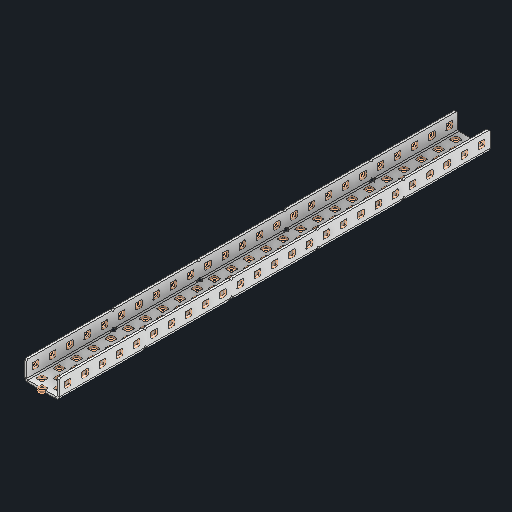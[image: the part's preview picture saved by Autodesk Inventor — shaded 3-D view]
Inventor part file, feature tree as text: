
AUTODESK INVENTOR PART (.ipt)
format: ipt  version: 2024 (Build 280153000, 153)  size: 2,048,000 bytes
history: native  units: in
note: dims shown in document units (in); Inventor stores cm internally (conversion verified against a paired STEP export)
features: other x256, sketch x5, sheet_metal_op x1
ambient origin geometry x8: Origin, YZ Plane, XZ Plane, XY Plane, X Axis, Y Axis, Z Axis, Center Point
bodies: Solid1 (feature_tree)
feature tree (262):
  other  "Alu C 1x2x1x25.ipt"
  other  "Solid1::Alu C 1x2x1x25.ipt"
  other  "TaggingFeature1"
  sketch  "Sketch1"  dims[d0=0.3937in]
  sketch  "Sketch2"  dims[d1=0.0625in]
  sketch  "Sketch3"
  other  "Flange Pattern Sketch"
  sketch  "Sketch9"
  sheet_metal_op  "Body Pattern Sketch"
  other  "Arc Length"
  sketch  "Sketch14"
  other  "Flange Pattern Plane"
  other  "Srf1"
  other  "Srf2"
  other  "Srf3"
  other  "Srf4"
  other  "Srf5"
  other  "Srf6"
  other  "Srf7"
  other  "Srf8"
  other  "Srf9"
  other  "Srf10"
  other  "Srf11"
  other  "Srf12"
  other  "Srf13"
  other  "Srf14"
  other  "Srf15"
  other  "Srf16"
  other  "Srf17"
  other  "Srf18"
  other  "Srf19"
  other  "Srf20"
  other  "Srf21"
  other  "Srf22"
  other  "Srf23"
  other  "Srf24"
  other  "Srf25"
  other  "Srf26"
  other  "Srf27"
  other  "Srf28"
  other  "Srf29"
  other  "Srf30"
  other  "Srf31"
  other  "Srf32"
  other  "Srf33"
  other  "Srf34"
  other  "Srf35"
  other  "Srf36"
  other  "Srf37"
  other  "Srf38"
  other  "Srf39"
  other  "Srf40"
  other  "Srf41"
  other  "Srf42"
  other  "Srf43"
  other  "Srf44"
  other  "Srf45"
  other  "Srf46"
  other  "Srf47"
  other  "Srf48"
  other  "Srf49"
  other  "Srf50"
  other  "Srf51"
  other  "Srf52"
  other  "Srf53"
  other  "Srf54"
  other  "Srf55"
  other  "Srf56"
  other  "Srf57"
  other  "Srf58"
  other  "Srf59"
  other  "Srf60"
  other  "Srf61"
  other  "Srf62"
  other  "Srf63"
  other  "Srf64"
  other  "Srf65"
  other  "Srf66"
  other  "Srf67"
  other  "Srf68"
  other  "Srf69"
  other  "Srf70"
  other  "Srf71"
  other  "Srf72"
  other  "Srf73"
  other  "Srf74"
  other  "Srf75"
  other  "Srf76"
  other  "Srf77"
  other  "Srf78"
  other  "Srf79"
  other  "Srf80"
  other  "Srf81"
  other  "Srf82"
  other  "Srf83"
  other  "Srf84"
  other  "Srf85"
  other  "Srf86"
  other  "Srf87"
  other  "Srf88"
  other  "Srf89"
  other  "Srf90"
  other  "Srf91"
  other  "Srf92"
  other  "Srf93"
  other  "Srf94"
  other  "Srf95"
  other  "Srf96"
  other  "Srf97"
  other  "Srf98"
  other  "Srf99"
  other  "Srf100"
  other  "Srf101"
  other  "Srf102"
  other  "Srf103"
  other  "Srf104"
  other  "Srf105"
  other  "Srf106"
  other  "Srf107"
  other  "Srf108"
  other  "Srf109"
  other  "Srf110"
  other  "Srf111"
  other  "Srf112"
  other  "Srf113"
  other  "Srf114"
  other  "Srf115"
  other  "Srf116"
  other  "Srf117"
  other  "Srf118"
  other  "Srf119"
  other  "Srf120"
  other  "Srf121"
  other  "Srf122"
  other  "Srf123"
  other  "Srf124"
  other  "Srf125"
  other  "Srf1::Derived"
  other  "Srf2::Derived"
  other  "Srf823::Derived"
  other  "Srf824::Derived"
  other  "Srf825::Derived"
  other  "Srf826::Derived"
  other  "Srf827::Derived"
  other  "Srf828::Derived"
  other  "Srf829::Derived"
  other  "Srf922::Derived"
  other  "Srf923::Derived"
  other  "Srf924::Derived"
  other  "Srf925::Derived"
  other  "Srf926::Derived"
  other  "Srf1143::Derived"
  other  "Srf1144::Derived"
  other  "Srf1145::Derived"
  other  "Srf1146::Derived"
  other  "Srf1147::Derived"
  other  "Srf1148::Derived"
  other  "Srf1149::Derived"
  other  "Srf1150::Derived"
  other  "Srf1151::Derived"
  other  "Srf1152::Derived"
  other  "Srf1153::Derived"
  other  "Srf1154::Derived"
  other  "Srf1155::Derived"
  other  "Srf1156::Derived"
  other  "Srf1157::Derived"
  other  "Srf1158::Derived"
  other  "Srf1159::Derived"
  other  "Srf1160::Derived"
  other  "Srf1161::Derived"
  other  "Srf1162::Derived"
  other  "Srf1163::Derived"
  other  "Srf1164::Derived"
  other  "Srf1165::Derived"
  other  "Srf1166::Derived"
  other  "Srf1167::Derived"
  other  "Srf1168::Derived"
  other  "Srf1169::Derived"
  other  "Srf1170::Derived"
  other  "Srf1171::Derived"
  other  "Srf1172::Derived"
  other  "Srf1173::Derived"
  other  "Srf1174::Derived"
  other  "Srf1175::Derived"
  other  "Srf1176::Derived"
  other  "Srf1177::Derived"
  other  "Srf1178::Derived"
  other  "Srf91::Derived"
  other  "Srf92::Derived"
  other  "Srf856::Derived"
  other  "Srf857::Derived"
  other  "Srf858::Derived"
  other  "Srf859::Derived"
  other  "Srf860::Derived"
  other  "Srf861::Derived"
  other  "Srf862::Derived"
  other  "Srf959::Derived"
  other  "Srf960::Derived"
  other  "Srf961::Derived"
  other  "Srf962::Derived"
  other  "Srf963::Derived"
  other  "Srf1199::Derived"
  other  "Srf1200::Derived"
  other  "Srf1201::Derived"
  other  "Srf1202::Derived"
  other  "Srf1203::Derived"
  other  "Srf1204::Derived"
  other  "Srf1205::Derived"
  other  "Srf1206::Derived"
  other  "Srf1207::Derived"
  other  "Srf1208::Derived"
  other  "Srf1209::Derived"
  other  "Srf1210::Derived"
  other  "Srf1211::Derived"
  other  "Srf1212::Derived"
  other  "Srf1213::Derived"
  other  "Srf1214::Derived"
  other  "Srf1215::Derived"
  other  "Srf1216::Derived"
  other  "Srf1217::Derived"
  other  "Srf1218::Derived"
  other  "Srf1219::Derived"
  other  "Srf1220::Derived"
  other  "Srf1221::Derived"
  other  "Srf1222::Derived"
  other  "Srf1223::Derived"
  other  "Srf1224::Derived"
  other  "Srf1225::Derived"
  other  "Srf1226::Derived"
  other  "Srf1227::Derived"
  other  "Srf1228::Derived"
  other  "Srf1229::Derived"
  other  "Srf1230::Derived"
  other  "Srf1231::Derived"
  other  "Srf1232::Derived"
  other  "Srf1233::Derived"
  other  "Srf1234::Derived"
  other  "Srf786::Derived"
  other  "Srf889::Derived"
  other  "Srf890::Derived"
  other  "Srf891::Derived"
  other  "Srf892::Derived"
  other  "Srf893::Derived"
  other  "Srf894::Derived"
  other  "Srf895::Derived"
  other  "Srf896::Derived"
  other  "Srf996::Derived"
  other  "Srf997::Derived"
  other  "Srf998::Derived"
  other  "Srf999::Derived"
  other  "Srf1000::Derived"
  other  "Srf1255::Derived"
  other  "Srf1256::Derived"
  other  "Srf1257::Derived"
  other  "Srf1258::Derived"
  other  "Srf1259::Derived"
  other  "Srf1260::Derived"
  other  "Srf1261::Derived"
  other  "Srf1262::Derived"
  other  "Srf1263::Derived"
  other  "Srf1264::Derived"
  other  "Srf1265::Derived"
